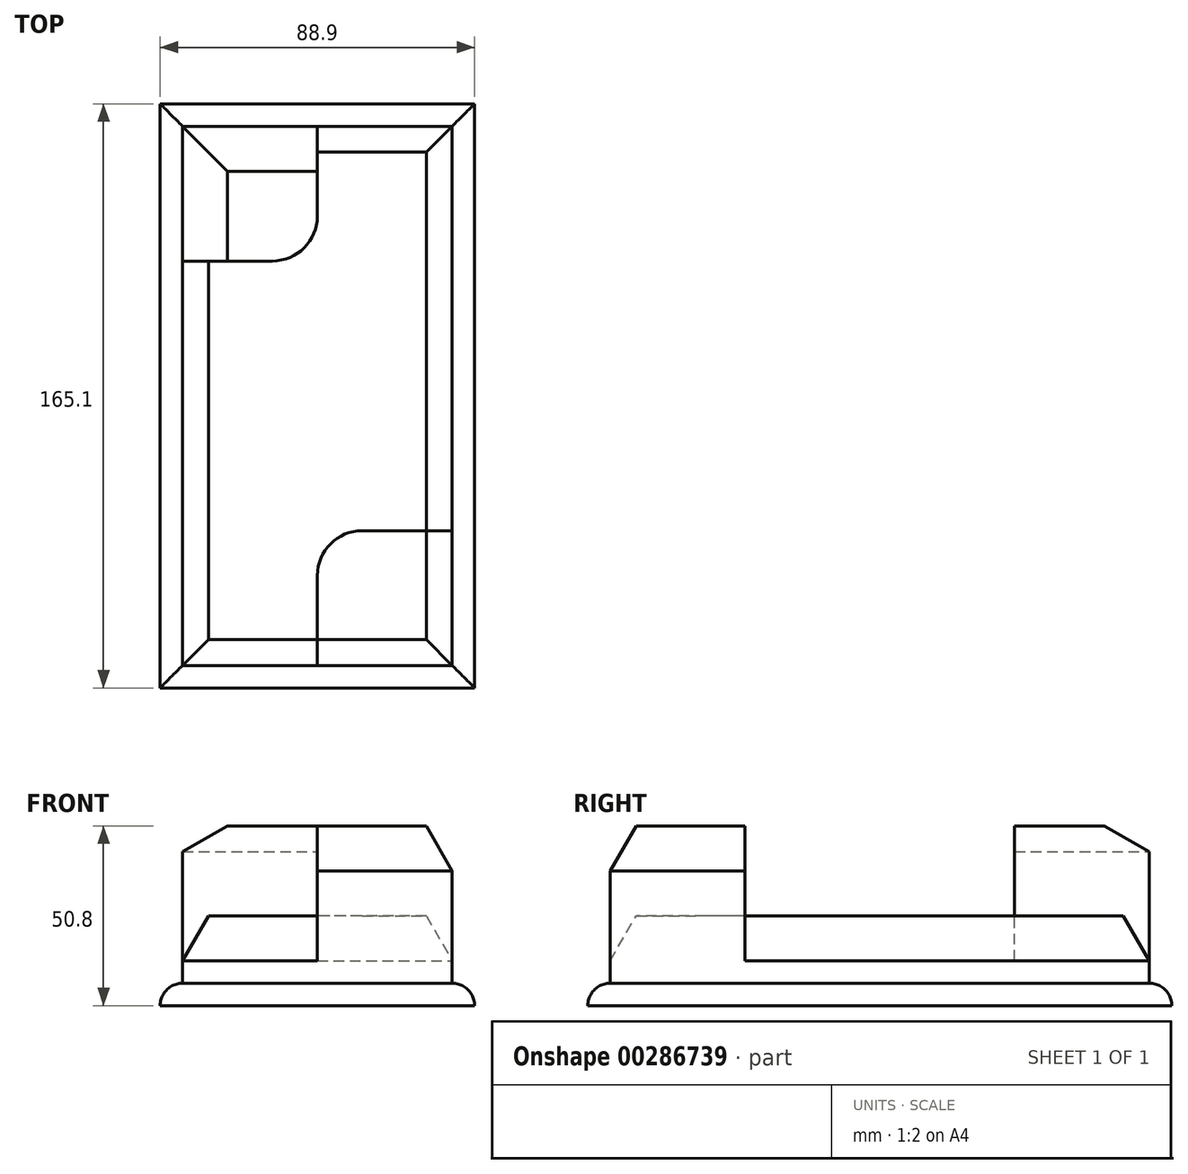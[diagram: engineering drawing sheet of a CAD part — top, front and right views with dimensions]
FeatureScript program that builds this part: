
annotation { "Feature Type Name" : "Feature", "Feature Type Description" : "" }
export const myFeature = defineFeature(function(context is Context, id is Id, definition is map)
    precondition{}
    {
        {
            var Q0;
            Q0=qCreatedBy(makeId("Top.planeOp"),FACE);
            var sketch = newSketch(context, id + "F0", { "sketchPlane" : qUnion([Q0])});
            skLineSegment(sketch, "E0.bottom", {"start": v(38.1, 76.2) * mm, "end": v(-38.1, 76.2) * mm});
            skLineSegment(sketch, "E0.top", {"start": v(38.1, -76.2) * mm, "end": v(-38.1, -76.2) * mm});
            skLineSegment(sketch, "E0.left", {"start": v(38.1, 76.2) * mm, "end": v(38.1, -76.2) * mm});
            skLineSegment(sketch, "E0.right", {"start": v(-38.1, 76.2) * mm, "end": v(-38.1, -76.2) * mm});
            skPoint(sketch, "E0.middle", {"position": v(0, 0) * mm});
            skLineSegment(sketch, "E1.bottom", {"start": v(44.45, 82.55) * mm, "end": v(-44.45, 82.55) * mm});
            skLineSegment(sketch, "E1.top", {"start": v(44.45, -82.55) * mm, "end": v(-44.45, -82.55) * mm});
            skLineSegment(sketch, "E1.left", {"start": v(44.45, 82.55) * mm, "end": v(44.45, -82.55) * mm});
            skLineSegment(sketch, "E1.right", {"start": v(-44.45, 82.55) * mm, "end": v(-44.45, -82.55) * mm});
            skLineSegment(sketch, "E2", {"start": v(0, -76.2) * mm, "end": v(0, -50.8) * mm});
            skPoint(sketch, "E2.endSnap0", {"position": v(0, -76.2) * mm});
            skLineSegment(sketch, "E3", {"start": v(12.7, -38.1) * mm, "end": v(38.1, -38.1) * mm});
            skPoint(sketch, "E4.visualSharp", {"position": v(0, -38.1) * mm});
            skArc(sketch, "E4.filletArc", {"start": v(12.7, -38.1) * mm, "mid": v(3.72, -41.82) * mm, "end": v(0, -50.8) * mm});
            skLineSegment(sketch, "E5", {"start": v(0, 76.2) * mm, "end": v(0, 50.8) * mm});
            skPoint(sketch, "E5.endSnap0", {"position": v(0, 76.2) * mm});
            skLineSegment(sketch, "E6", {"start": v(-12.7, 38.1) * mm, "end": v(-38.1, 38.1) * mm});
            skPoint(sketch, "E7.visualSharp", {"position": v(0, 38.1) * mm});
            skArc(sketch, "E7.filletArc", {"start": v(-12.7, 38.1) * mm, "mid": v(-3.72, 41.82) * mm, "end": v(0, 50.8) * mm});
            skSolve(sketch);
        }
        {
            var Q0;
            {var subQ9=sQuery(id+"F0.wireOp",EDGE,"E2");Q0=makeQuery(id+"F0.imprint","IMPRINT",FACE,{"disambiguationData":[TD([[makeQuery(id+"F0.imprint","IMPRINT",EDGE,{"derivedFrom":subQ9}),1.0]])]});}
            extrude(context, id + "F1", {"entities" : qUnion([Q0]), "depth" : 25.4 * mm});
        }
        {
            var Q0;
            Q0=makeQuery(id+"F0.imprint","IMPRINT",FACE,{"disambiguationData":[TD([[makeQuery(id+"F0.imprint","IMPRINT",EDGE,{"derivedFrom":sQuery(id+"F0.wireOp",EDGE,"E1.bottom")}),1.0]])]});
            extrude(context, id + "F2", {"entities" : qUnion([Q0]), "operationType" : NewBodyOperationType.ADD, "depth" : 6.35 * mm});
        }
        {
            var Q0;
            {var subQ4=sQuery(id+"F0.wireOp",EDGE,"E2");Q0=makeQuery(id+"F0.imprint","IMPRINT",FACE,{"disambiguationData":[TD([[makeQuery(id+"F0.imprint","IMPRINT",EDGE,{"derivedFrom":subQ4}),-1.0]])]});}
            var Q1;
            {var subQ0=sQuery(id+"F0.wireOp",EDGE,"E5");Q1=makeQuery(id+"F0.imprint","IMPRINT",FACE,{"disambiguationData":[TD([[makeQuery(id+"F0.imprint","IMPRINT",EDGE,{"derivedFrom":subQ0}),-1.0]])]});}
            extrude(context, id + "F3", {"entities" : qUnion([Q0, Q1]), "operationType" : NewBodyOperationType.ADD, "depth" : 50.8 * mm});
        }
        {
            var Q0;
            Q0=makeQuery(id+"F2.opExtrude","CAP_EDGE",EDGE,{"disambiguationData":[OSD([sQuery(id+"F0.wireOp",EDGE,"E1.right")])],"isStart":false});
            var Q1;
            Q1=makeQuery(id+"F2.opExtrude","CAP_EDGE",EDGE,{"disambiguationData":[OSD([sQuery(id+"F0.wireOp",EDGE,"E1.bottom")])],"isStart":false});
            var Q2;
            Q2=makeQuery(id+"F2.opExtrude","CAP_EDGE",EDGE,{"disambiguationData":[OSD([sQuery(id+"F0.wireOp",EDGE,"E1.left")])],"isStart":false});
            var Q3;
            Q3=makeQuery(id+"F2.opExtrude","CAP_EDGE",EDGE,{"disambiguationData":[OSD([sQuery(id+"F0.wireOp",EDGE,"E1.top")])],"isStart":false});
            fillet(context, id + "F4", {"entities" : qUnion([Q0, Q1, Q2, Q3]), "radius" : 6.35 * mm, "tangentPropagation" : true, "allowEdgeOverflow" : false});
        }
        {
            var Q0;
            Q0=makeQuery(id+"F1.opExtrude","CAP_EDGE",EDGE,{"disambiguationData":[OSD([sQuery(id+"F0.wireOp",EDGE,"E0.left")])],"isStart":false});
            var Q1;
            Q1=makeQuery(id+"F1.opExtrude","CAP_EDGE",EDGE,{"disambiguationData":[OSD([sQuery(id+"F0.wireOp",EDGE,"E0.bottom")])],"isStart":false});
            var Q2;
            Q2=makeQuery(id+"F1.opExtrude","CAP_EDGE",EDGE,{"disambiguationData":[OSD([sQuery(id+"F0.wireOp",EDGE,"E0.right")])],"isStart":false});
            var Q3;
            Q3=makeQuery(id+"F1.opExtrude","CAP_EDGE",EDGE,{"disambiguationData":[OSD([sQuery(id+"F0.wireOp",EDGE,"E0.top")])],"isStart":false});
            var Q4;
            Q4=makeQuery(id+"F3.opExtrude","CAP_EDGE",EDGE,{"disambiguationData":[OSD([sQuery(id+"F0.wireOp",EDGE,"E0.top")])],"isStart":false});
            var Q5;
            Q5=makeQuery(id+"F3.opExtrude","CAP_EDGE",EDGE,{"disambiguationData":[OSD([sQuery(id+"F0.wireOp",EDGE,"E0.left")])],"isStart":false});
            var Q6;
            Q6=makeQuery(id+"F3.opExtrude","CAP_EDGE",EDGE,{"disambiguationData":[OSD([sQuery(id+"F0.wireOp",EDGE,"E0.right")])],"isStart":false});
            var Q7;
            Q7=makeQuery(id+"F3.opExtrude","CAP_EDGE",EDGE,{"disambiguationData":[OSD([sQuery(id+"F0.wireOp",EDGE,"E0.bottom")])],"isStart":false});
            chamfer(context, id + "F5", {"entities" : qUnion([Q0, Q1, Q2, Q3, Q4, Q5, Q6, Q7]), "chamferType" : ChamferType.OFFSET_ANGLE, "width" : 12.7 * mm, "oppositeDirection" : false, "angle" : 30 * degree, "tangentPropagation" : true});
        }
    });
